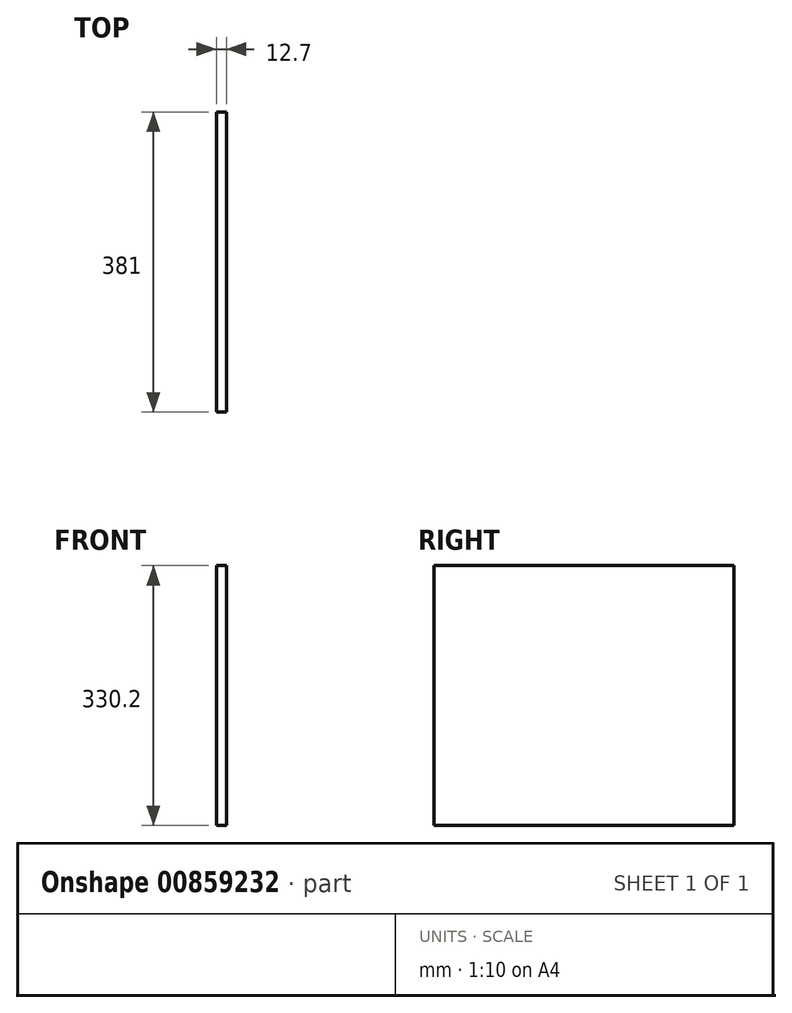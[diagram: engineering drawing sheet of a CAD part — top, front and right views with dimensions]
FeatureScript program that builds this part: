
annotation { "Feature Type Name" : "Feature", "Feature Type Description" : "" }
export const myFeature = defineFeature(function(context is Context, id is Id, definition is map)
    precondition{}
    {
        {
            var Q0;
            Q0=qCreatedBy(makeId("Right.planeOp"),FACE);
            var sketch = newSketch(context, id + "F0", { "sketchPlane" : qUnion([Q0])});
            skLineSegment(sketch, "E0.bottom", {"start": v(0, 0) * mm, "end": v(381, 0) * mm});
            skLineSegment(sketch, "E0.top", {"start": v(0, 330.2) * mm, "end": v(381, 330.2) * mm});
            skLineSegment(sketch, "E0.left", {"start": v(0, 0) * mm, "end": v(0, 330.2) * mm});
            skLineSegment(sketch, "E0.right", {"start": v(381, 0) * mm, "end": v(381, 330.2) * mm});
            skSolve(sketch);
        }
        {
            var Q0;
            Q0=makeQuery(id+"F0.imprint","IMPRINT",FACE,{"disambiguationData":[TD([[makeQuery(id+"F0.imprint","IMPRINT",EDGE,{"derivedFrom":sQuery(id+"F0.wireOp",EDGE,"E0.bottom")}),1.0]])]});
            extrude(context, id + "F1", {"entities" : qUnion([Q0]), "depth" : 12.7 * mm, "offsetDistance" : 25.4 * mm});
        }
    });
